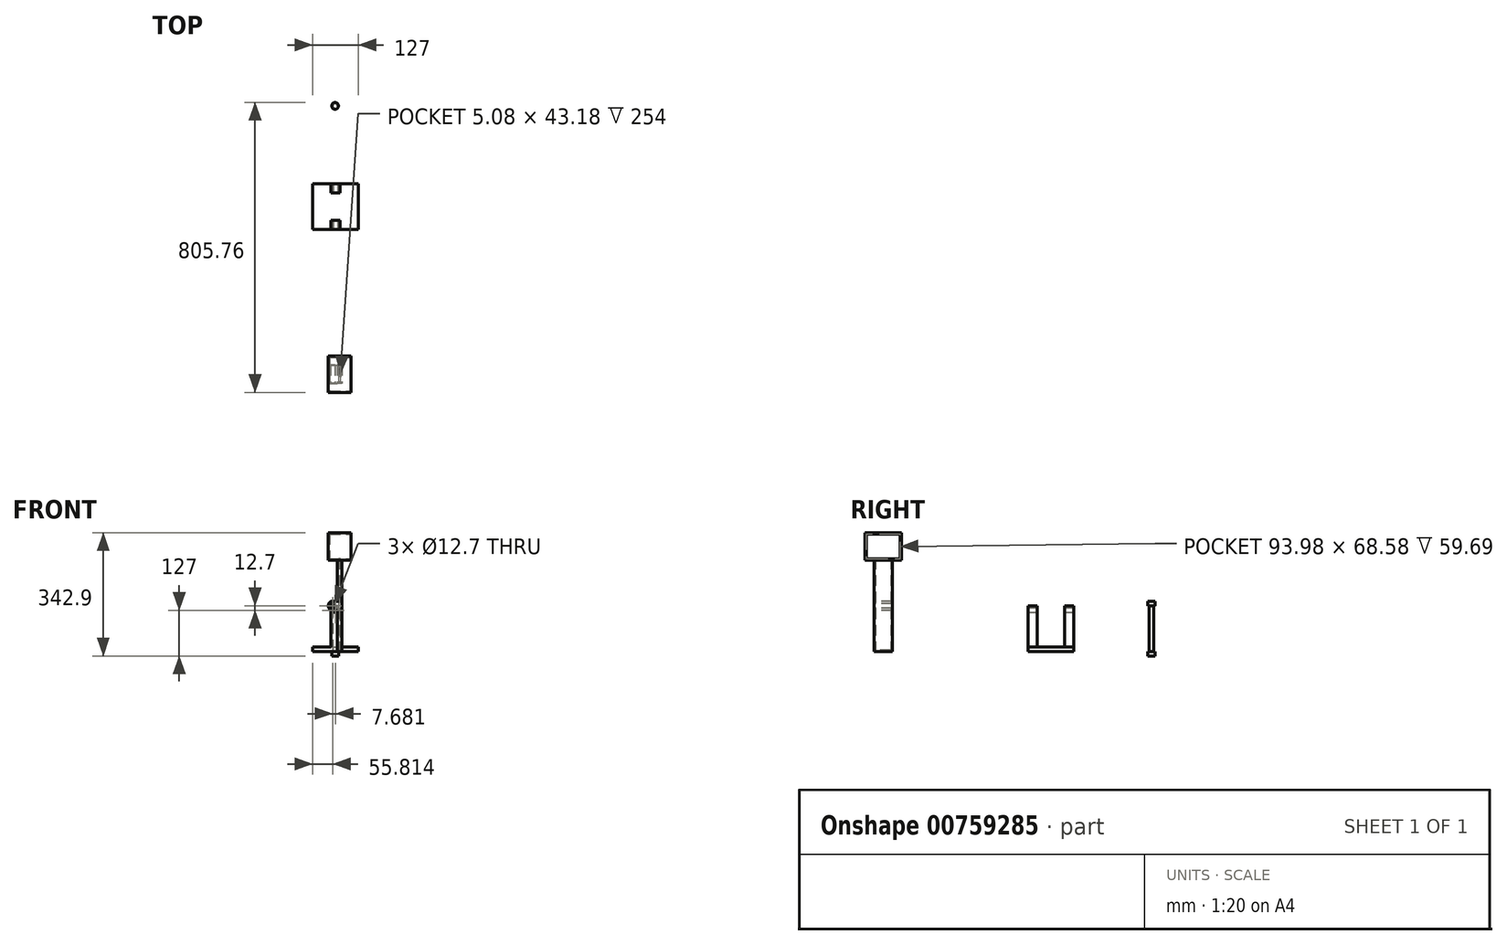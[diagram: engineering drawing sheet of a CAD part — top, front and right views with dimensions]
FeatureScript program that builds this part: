
annotation { "Feature Type Name" : "Feature", "Feature Type Description" : "" }
export const myFeature = defineFeature(function(context is Context, id is Id, definition is map)
    precondition{}
    {
        {
            var Q0;
            Q0=qCreatedBy(makeId("Top.planeOp"),FACE);
            var sketch = newSketch(context, id + "F0", { "sketchPlane" : qUnion([Q0])});
            skLineSegment(sketch, "E0.bottom", {"start": v(-62.3, 72.06) * mm, "end": v(64.7, 72.06) * mm});
            skLineSegment(sketch, "E0.top", {"start": v(-62.3, -54.94) * mm, "end": v(64.7, -54.94) * mm});
            skLineSegment(sketch, "E0.left", {"start": v(-62.3, 72.06) * mm, "end": v(-62.3, -54.94) * mm});
            skLineSegment(sketch, "E0.right", {"start": v(64.7, 72.06) * mm, "end": v(64.7, -54.94) * mm});
            skCircle(sketch, "E1", {"center": v(0, 288.32) * mm, "radius": 6.35 * mm});
            skLineSegment(sketch, "E2.bottom", {"start": v(18.92, -431.71) * mm, "end": v(6.22, -431.71) * mm});
            skLineSegment(sketch, "E2.top", {"start": v(18.92, -482.51) * mm, "end": v(6.22, -482.51) * mm});
            skLineSegment(sketch, "E2.left", {"start": v(18.92, -431.71) * mm, "end": v(18.92, -482.51) * mm});
            skLineSegment(sketch, "E2.right", {"start": v(6.22, -431.71) * mm, "end": v(6.22, -482.51) * mm});
            skPoint(sketch, "E2.middle", {"position": v(12.57, -457.11) * mm});
            skSolve(sketch);
        }
        {
            var Q0;
            Q0=makeQuery(id+"F0.imprint","IMPRINT",FACE,{"disambiguationData":[TD([[makeQuery(id+"F0.imprint","IMPRINT",EDGE,{"derivedFrom":sQuery(id+"F0.wireOp",EDGE,"E0.bottom")}),-1.0]])]});
            extrude(context, id + "F1", {"entities" : qUnion([Q0]), "depth" : 12.7 * mm, "offsetDistance" : 25.4 * mm});
        }
        {
            var Q0;
            Q0=makeQuery(id+"F1.opExtrude","CAP_FACE",FACE,{"disambiguationData":[OSD([sQuery(id+"F0.wireOp",EDGE,"E0.bottom"),sQuery(id+"F0.wireOp",EDGE,"E0.top"),sQuery(id+"F0.wireOp",EDGE,"E0.left"),sQuery(id+"F0.wireOp",EDGE,"E0.right")])],"isStart":false});
            var sketch = newSketch(context, id + "F2", { "sketchPlane" : qUnion([Q0])});
            skPoint(sketch, "E3.firstSnap0", {"position": v(1.2, 72.06) * mm});
            skLineSegment(sketch, "E4.bottom", {"start": v(13.9, -54.94) * mm, "end": v(-11.5, -54.94) * mm});
            skLineSegment(sketch, "E4.top", {"start": v(13.9, -29.54) * mm, "end": v(-11.5, -29.54) * mm});
            skLineSegment(sketch, "E4.left", {"start": v(13.9, -54.94) * mm, "end": v(13.9, -29.54) * mm});
            skLineSegment(sketch, "E4.right", {"start": v(-11.5, -54.94) * mm, "end": v(-11.5, -29.54) * mm});
            skPoint(sketch, "E4.middle", {"position": v(1.2, -42.24) * mm});
            skLineSegment(sketch, "E5.bottom", {"start": v(-11.5, 72.06) * mm, "end": v(13.9, 72.06) * mm});
            skLineSegment(sketch, "E5.top", {"start": v(-11.5, 46.66) * mm, "end": v(13.9, 46.66) * mm});
            skLineSegment(sketch, "E5.left", {"start": v(-11.5, 72.06) * mm, "end": v(-11.5, 46.66) * mm});
            skLineSegment(sketch, "E5.right", {"start": v(13.9, 72.06) * mm, "end": v(13.9, 46.66) * mm});
            skPoint(sketch, "E5.middle", {"position": v(1.2, 59.36) * mm});
            skPoint(sketch, "E5.middle.positionSnap0", {"position": v(1.2, -29.54) * mm});
            skPoint(sketch, "E5.centerSnap0", {"position": v(1.2, -29.54) * mm});
            skSolve(sketch);
        }
        {
            var Q0;
            Q0=qSketchRegion(id+"F2",true);
            extrude(context, id + "F3", {"entities" : qUnion([Q0]), "operationType" : NewBodyOperationType.ADD, "depth" : 114.3 * mm, "offsetDistance" : 25.4 * mm});
        }
        {
            var Q0;
            Q0=makeQuery(id+"F3.opExtrude","CAP_EDGE",EDGE,{"disambiguationData":[OSD([sQuery(id+"F2.wireOp",EDGE,"E4.left")])],"isStart":false});
            fillet(context, id + "F4", {"entities" : qUnion([Q0]), "radius" : 12.7 * mm, "tangentPropagation" : true, "allowEdgeOverflow" : false});
        }
        {
            var Q0;
            Q0=makeQuery(id+"F3.opExtrude","CAP_EDGE",EDGE,{"disambiguationData":[OSD([sQuery(id+"F2.wireOp",EDGE,"E4.right")])],"isStart":false});
            fillet(context, id + "F5", {"entities" : qUnion([Q0]), "radius" : 12.7 * mm, "tangentPropagation" : true, "allowEdgeOverflow" : false});
        }
        {
            var Q0;
            Q0=makeQuery(id+"F3.opExtrude","CAP_EDGE",EDGE,{"disambiguationData":[OSD([sQuery(id+"F2.wireOp",EDGE,"E5.left")])],"isStart":false});
            var Q1;
            Q1=makeQuery(id+"F3.opExtrude","CAP_EDGE",EDGE,{"disambiguationData":[OSD([sQuery(id+"F2.wireOp",EDGE,"E5.right")])],"isStart":false});
            fillet(context, id + "F6", {"entities" : qUnion([Q0, Q1]), "radius" : 12.7 * mm, "tangentPropagation" : true, "allowEdgeOverflow" : false});
        }
        {
            var Q0;
            Q0=makeQuery(id+"F3.boolean.opBoolean","MERGE",FACE,{"derivedFrom":[makeQuery(id+"F1.opExtrude","SWEPT_FACE",FACE,{"disambiguationData":[OSD([sQuery(id+"F0.wireOp",EDGE,"E0.top")])]}),makeQuery(id+"F3.opExtrude","SWEPT_FACE",FACE,{"disambiguationData":[OSD([sQuery(id+"F2.wireOp",EDGE,"E4.bottom")])]})]});
            var sketch = newSketch(context, id + "F7", { "sketchPlane" : qUnion([Q0])});
            skCircle(sketch, "E6", {"center": v(1.2, 114.3) * mm, "radius": 6.35 * mm});
            skSolve(sketch);
        }
        {
            var Q0;
            Q0=makeQuery(id+"F7.imprint","IMPRINT",FACE,{"disambiguationData":[TD([[makeQuery(id+"F7.imprint","IMPRINT",EDGE,{"derivedFrom":sQuery(id+"F7.wireOp",EDGE,"E6")}),1.0]])]});
            extrude(context, id + "F8", {"entities" : qUnion([Q0]), "operationType" : NewBodyOperationType.REMOVE, "oppositeDirection" : true, "depth" : 153.42 * mm, "offsetDistance" : 25.4 * mm});
        }
        {
            var Q0;
            Q0=makeQuery(id+"F0.imprint","IMPRINT",FACE,{"disambiguationData":[TD([[makeQuery(id+"F0.imprint","IMPRINT",EDGE,{"derivedFrom":sQuery(id+"F0.wireOp",EDGE,"E1")}),1.0]])]});
            extrude(context, id + "F9", {"entities" : qUnion([Q0]), "depth" : 127 * mm, "offsetDistance" : 25.4 * mm});
        }
        {
            var Q0;
            Q0=makeQuery(id+"F9.opExtrude","CAP_FACE",FACE,{"disambiguationData":[OSD([sQuery(id+"F0.wireOp",EDGE,"E1")])],"isStart":false});
            var sketch = newSketch(context, id + "F10", { "sketchPlane" : qUnion([Q0])});
            skCircle(sketch, "E7", {"center": v(0, 288.32) * mm, "radius": 9.53 * mm});
            skSolve(sketch);
        }
        {
            var Q0;
            Q0=qSketchRegion(id+"F10",true);
            extrude(context, id + "F11", {"entities" : qUnion([Q0]), "operationType" : NewBodyOperationType.ADD, "depth" : 12.7 * mm, "offsetDistance" : 25.4 * mm});
        }
        {
            var Q0;
            Q0=makeQuery(id+"F9.opExtrude","CAP_FACE",FACE,{"disambiguationData":[OSD([sQuery(id+"F0.wireOp",EDGE,"E1")])],"isStart":true});
            var sketch = newSketch(context, id + "F12", { "sketchPlane" : qUnion([Q0])});
            skCircle(sketch, "E8", {"center": v(0, -288.32) * mm, "radius": 9.53 * mm});
            skSolve(sketch);
        }
        {
            var Q0;
            Q0=qSketchRegion(id+"F12",true);
            extrude(context, id + "F13", {"entities" : qUnion([Q0]), "operationType" : NewBodyOperationType.ADD, "depth" : 12.7 * mm, "offsetDistance" : 25.4 * mm});
        }
        {
            var Q0;
            Q0=makeQuery(id+"F0.imprint","IMPRINT",FACE,{"disambiguationData":[TD([[makeQuery(id+"F0.imprint","IMPRINT",EDGE,{"derivedFrom":sQuery(id+"F0.wireOp",EDGE,"E2.bottom")}),1.0]])]});
            extrude(context, id + "F14", {"entities" : qUnion([Q0]), "depth" : 254 * mm, "offsetDistance" : 25.4 * mm});
        }
        {
            var Q0;
            Q0=makeQuery(id+"F14.opExtrude","CAP_FACE",FACE,{"disambiguationData":[OSD([sQuery(id+"F0.wireOp",EDGE,"E2.bottom"),sQuery(id+"F0.wireOp",EDGE,"E2.top"),sQuery(id+"F0.wireOp",EDGE,"E2.left"),sQuery(id+"F0.wireOp",EDGE,"E2.right")])],"isStart":false});
            var sketch = newSketch(context, id + "F15", { "sketchPlane" : qUnion([Q0])});
            skLineSegment(sketch, "E9.bottom", {"start": v(-19.18, -406.31) * mm, "end": v(44.32, -406.31) * mm});
            skLineSegment(sketch, "E9.top", {"start": v(-19.18, -507.91) * mm, "end": v(44.32, -507.91) * mm});
            skLineSegment(sketch, "E9.left", {"start": v(-19.18, -406.31) * mm, "end": v(-19.18, -507.91) * mm});
            skLineSegment(sketch, "E9.right", {"start": v(44.32, -406.31) * mm, "end": v(44.32, -507.91) * mm});
            skPoint(sketch, "E9.middle", {"position": v(12.57, -457.11) * mm});
            skPoint(sketch, "E9.middle.positionSnap0", {"position": v(12.57, -431.71) * mm});
            skPoint(sketch, "E9.middle.positionSnap1", {"position": v(6.22, -457.11) * mm});
            skPoint(sketch, "E9.centerSnap0", {"position": v(12.57, -431.71) * mm});
            skPoint(sketch, "E9.centerSnap1", {"position": v(6.22, -457.11) * mm});
            skSolve(sketch);
        }
        {
            var Q0;
            Q0=makeQuery(id+"F15.imprint","IMPRINT",FACE,{"disambiguationData":[TD([[makeQuery(id+"F15.imprint","IMPRINT",EDGE,{"derivedFrom":makeQuery(id+"F14.opExtrude","CAP_EDGE",EDGE,{"disambiguationData":[OSD([sQuery(id+"F0.wireOp",EDGE,"E2.bottom")])],"isStart":false})}),1.0]])]});
            var Q1;
            Q1=makeQuery(id+"F15.imprint","IMPRINT",FACE,{"disambiguationData":[TD([[makeQuery(id+"F15.imprint","IMPRINT",EDGE,{"derivedFrom":sQuery(id+"F15.wireOp",EDGE,"E9.bottom")}),-1.0]])]});
            extrude(context, id + "F16", {"entities" : qUnion([Q0, Q1]), "operationType" : NewBodyOperationType.ADD, "depth" : 76.2 * mm, "offsetDistance" : 25.4 * mm});
        }
        {
            var Q0;
            Q0=makeQuery(id+"F16.opExtrude","SWEPT_FACE",FACE,{"disambiguationData":[OSD([sQuery(id+"F15.wireOp",EDGE,"E9.right")])]});
            shell(context, id + "F17", {"entities" : qUnion([Q0]), "thickness" : 3.8 * mm});
        }
        {
            var Q0;
            Q0=makeQuery(id+"F14.opExtrude","SWEPT_FACE",FACE,{"disambiguationData":[OSD([sQuery(id+"F0.wireOp",EDGE,"E2.right")])]});
            var sketch = newSketch(context, id + "F18", { "sketchPlane" : qUnion([Q0])});
            skPoint(sketch, "E10.middle", {"position": v(457.11, 127) * mm});
            skPoint(sketch, "E10.middle.positionSnap0", {"position": v(457.11, 0) * mm});
            skPoint(sketch, "E10.middle.positionSnap1", {"position": v(431.71, 127) * mm});
            skPoint(sketch, "E10.centerSnap0", {"position": v(457.11, 0) * mm});
            skPoint(sketch, "E10.centerSnap1", {"position": v(431.71, 127) * mm});
            skLineSegment(sketch, "E11.bottom", {"start": v(431.71, 139.7) * mm, "end": v(482.51, 139.7) * mm});
            skLineSegment(sketch, "E11.top", {"start": v(431.71, 114.3) * mm, "end": v(482.51, 114.3) * mm});
            skLineSegment(sketch, "E11.left", {"start": v(431.71, 139.7) * mm, "end": v(431.71, 114.3) * mm});
            skLineSegment(sketch, "E11.right", {"start": v(482.51, 139.7) * mm, "end": v(482.51, 114.3) * mm});
            skSolve(sketch);
        }
        {
            var Q0;
            Q0=makeQuery(id+"F18.imprint","IMPRINT",FACE,{"disambiguationData":[TD([[makeQuery(id+"F18.imprint","IMPRINT",EDGE,{"derivedFrom":sQuery(id+"F18.wireOp",EDGE,"E11.bottom")}),-1.0]])]});
            extrude(context, id + "F19", {"entities" : qUnion([Q0]), "operationType" : NewBodyOperationType.ADD, "depth" : 25.4 * mm, "offsetDistance" : 25.4 * mm});
        }
        {
            var Q0;
            Q0=makeQuery(id+"F19.opExtrude","CAP_EDGE",EDGE,{"disambiguationData":[OSD([sQuery(id+"F18.wireOp",EDGE,"E11.top")])],"isStart":false});
            var Q1;
            Q1=makeQuery(id+"F19.opExtrude","CAP_EDGE",EDGE,{"disambiguationData":[OSD([sQuery(id+"F18.wireOp",EDGE,"E11.bottom")])],"isStart":false});
            fillet(context, id + "F20", {"entities" : qUnion([Q0, Q1]), "radius" : 12.7 * mm, "tangentPropagation" : true, "allowEdgeOverflow" : false});
        }
        {
            var Q0;
            Q0=makeQuery(id+"F19.boolean.opBoolean","MERGE",FACE,{"derivedFrom":[makeQuery(id+"F14.opExtrude","SWEPT_FACE",FACE,{"disambiguationData":[OSD([sQuery(id+"F0.wireOp",EDGE,"E2.top")])]}),makeQuery(id+"F19.opExtrude","SWEPT_FACE",FACE,{"disambiguationData":[OSD([sQuery(id+"F18.wireOp",EDGE,"E11.right")])]})]});
            var sketch = newSketch(context, id + "F21", { "sketchPlane" : qUnion([Q0])});
            skCircle(sketch, "E12", {"center": v(-6.48, 127) * mm, "radius": 6.35 * mm});
            skSolve(sketch);
        }
        {
            var Q0;
            Q0=makeQuery(id+"F21.imprint","IMPRINT",FACE,{"disambiguationData":[TD([[makeQuery(id+"F21.imprint","IMPRINT",EDGE,{"derivedFrom":sQuery(id+"F21.wireOp",EDGE,"E12")}),1.0]])]});
            extrude(context, id + "F22", {"entities" : qUnion([Q0]), "operationType" : NewBodyOperationType.REMOVE, "oppositeDirection" : true, "depth" : 80 * mm, "offsetDistance" : 25.4 * mm});
        }
    });
